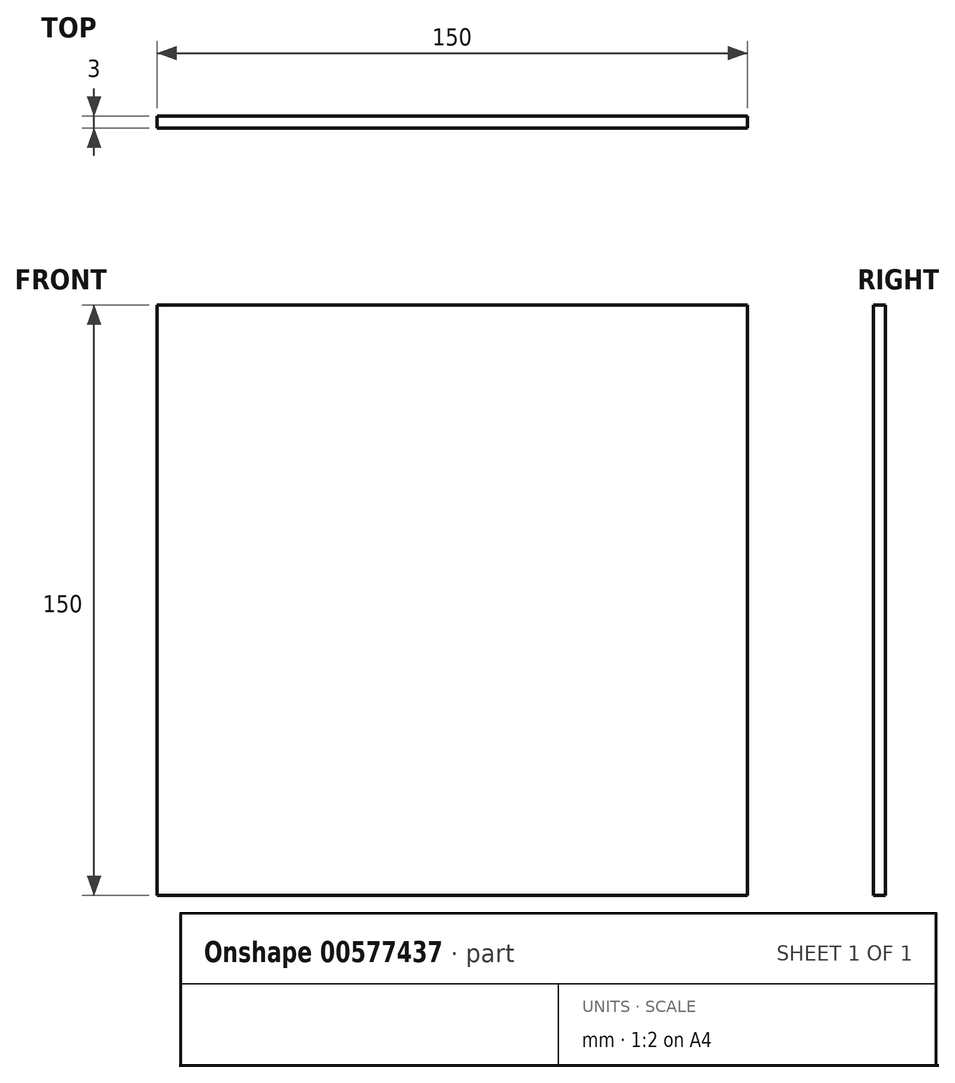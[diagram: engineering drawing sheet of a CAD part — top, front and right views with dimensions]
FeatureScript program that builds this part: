
annotation { "Feature Type Name" : "Feature", "Feature Type Description" : "" }
export const myFeature = defineFeature(function(context is Context, id is Id, definition is map)
    precondition{}
    {
        {
            var Q0;
            Q0=qCreatedBy(makeId("Front.planeOp"),FACE);
            var sketch = newSketch(context, id + "F0", { "sketchPlane" : qUnion([Q0])});
            skLineSegment(sketch, "E0.bottom", {"start": v(0, 0) * mm, "end": v(150, 0) * mm});
            skLineSegment(sketch, "E0.top", {"start": v(0, 150) * mm, "end": v(150, 150) * mm});
            skLineSegment(sketch, "E0.left", {"start": v(0, 0) * mm, "end": v(0, 150) * mm});
            skLineSegment(sketch, "E0.right", {"start": v(150, 0) * mm, "end": v(150, 150) * mm});
            skSolve(sketch);
        }
        {
            var Q0;
            Q0 = qSketchRegion(id + "F0", true);
            extrude(context, id + "F1", {"entities" : qUnion([Q0]), "oppositeDirection" : true, "depth" : 3 * mm, "offsetDistance" : 25 * mm});
        }
    });
